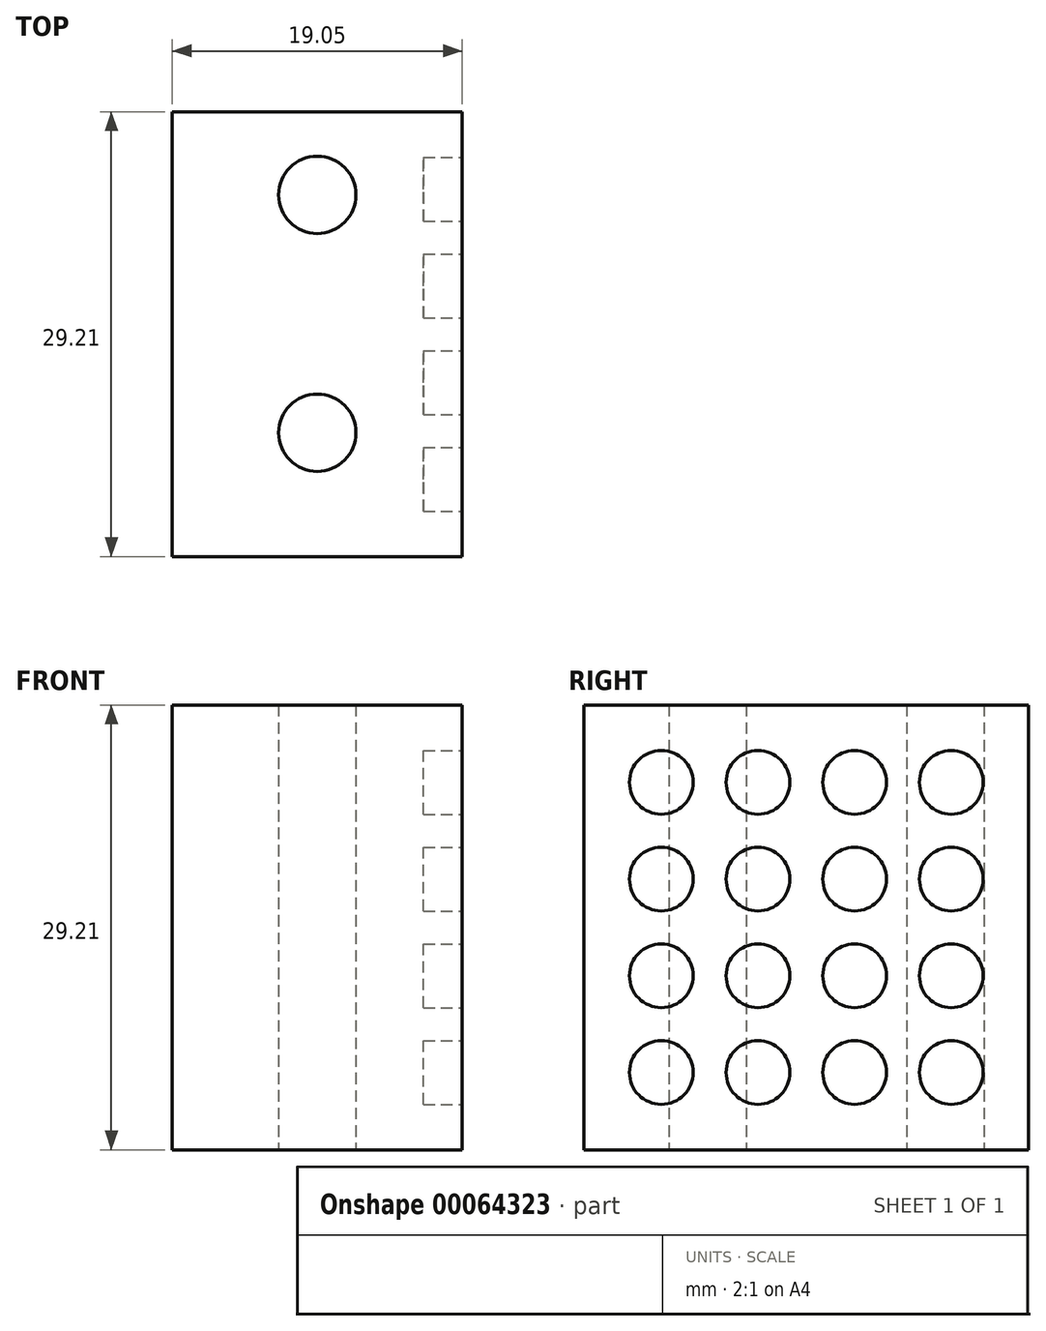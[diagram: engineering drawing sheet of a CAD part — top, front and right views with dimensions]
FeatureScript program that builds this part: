
annotation { "Feature Type Name" : "Feature", "Feature Type Description" : "" }
export const myFeature = defineFeature(function(context is Context, id is Id, definition is map)
    precondition{}
    {
        {
            var Q0;
            Q0=qCreatedBy(makeId("Top.planeOp"),FACE);
            var sketch = newSketch(context, id + "F0", { "sketchPlane" : qUnion([Q0])});
            skLineSegment(sketch, "E0.bottom", {"start": v(0, 0) * mm, "end": v(-19.05, 0) * mm});
            skLineSegment(sketch, "E0.top", {"start": v(0, 29.21) * mm, "end": v(-19.05, 29.21) * mm});
            skLineSegment(sketch, "E0.left", {"start": v(0, 0) * mm, "end": v(0, 29.21) * mm});
            skLineSegment(sketch, "E0.right", {"start": v(-19.05, 0) * mm, "end": v(-19.05, 29.21) * mm});
            skCircle(sketch, "E1", {"center": v(-9.53, 23.75) * mm, "radius": 2.54 * mm});
            skCircle(sketch, "E2", {"center": v(-9.53, 8.13) * mm, "radius": 2.54 * mm});
            skLineSegment(sketch, "E3", {"start": v(-9.53, 29.21) * mm, "end": v(-9.53, 0) * mm, "construction": true});
            skSolve(sketch);
        }
        {
            var Q0;
            Q0 = qSketchRegion(id + "F0", true);
            extrude(context, id + "F1", {"entities" : qUnion([Q0]), "depth" : 29.2 * mm});
        }
        {
            var Q0;
            Q0=makeQuery(id+"F1.opExtrude","SWEPT_FACE",FACE,{"disambiguationData":[OSD([sQuery(id+"F0.wireOp",EDGE,"E0.left")])]});
            var sketch = newSketch(context, id + "F2", { "sketchPlane" : qUnion([Q0])});
            skCircle(sketch, "E4", {"center": v(5.08, 24.13) * mm, "radius": 2.1 * mm});
            skCircle(sketch, "E5.1.0.0", {"center": v(11.43, 24.13) * mm, "radius": 2.1 * mm});
            skCircle(sketch, "E5.2.0.0", {"center": v(17.78, 24.13) * mm, "radius": 2.1 * mm});
            skCircle(sketch, "E5.3.0.0", {"center": v(24.13, 24.13) * mm, "radius": 2.1 * mm});
            skLineSegment(sketch, "E5.direction1", {"start": v(5.08, 24.13) * mm, "end": v(11.43, 24.13) * mm, "construction": true});
            skLineSegment(sketch, "E6.1.0.0", {"start": v(5.08, 17.78) * mm, "end": v(11.43, 17.78) * mm, "construction": true});
            skCircle(sketch, "E6.1.0.1", {"center": v(24.13, 17.78) * mm, "radius": 2.1 * mm});
            skCircle(sketch, "E6.1.0.2", {"center": v(17.78, 17.78) * mm, "radius": 2.1 * mm});
            skCircle(sketch, "E6.1.0.3", {"center": v(11.43, 17.78) * mm, "radius": 2.1 * mm});
            skCircle(sketch, "E6.1.0.4", {"center": v(5.08, 17.78) * mm, "radius": 2.1 * mm});
            skLineSegment(sketch, "E6.2.0.0", {"start": v(5.08, 11.43) * mm, "end": v(11.43, 11.43) * mm, "construction": true});
            skCircle(sketch, "E6.2.0.1", {"center": v(24.13, 11.43) * mm, "radius": 2.1 * mm});
            skCircle(sketch, "E6.2.0.2", {"center": v(17.78, 11.43) * mm, "radius": 2.1 * mm});
            skCircle(sketch, "E6.2.0.3", {"center": v(11.43, 11.43) * mm, "radius": 2.1 * mm});
            skCircle(sketch, "E6.2.0.4", {"center": v(5.08, 11.43) * mm, "radius": 2.1 * mm});
            skLineSegment(sketch, "E6.3.0.0", {"start": v(5.08, 5.08) * mm, "end": v(11.43, 5.08) * mm, "construction": true});
            skCircle(sketch, "E6.3.0.1", {"center": v(24.13, 5.08) * mm, "radius": 2.1 * mm});
            skCircle(sketch, "E6.3.0.2", {"center": v(17.78, 5.08) * mm, "radius": 2.1 * mm});
            skCircle(sketch, "E6.3.0.3", {"center": v(11.43, 5.08) * mm, "radius": 2.1 * mm});
            skCircle(sketch, "E6.3.0.4", {"center": v(5.08, 5.08) * mm, "radius": 2.1 * mm});
            skLineSegment(sketch, "E6.direction1", {"start": v(5.08, 24.13) * mm, "end": v(5.08, 17.78) * mm, "construction": true});
            skSolve(sketch);
        }
        {
            var Q0;
            Q0 = qSketchRegion(id + "F2", true);
            extrude(context, id + "F3", {"entities" : qUnion([Q0]), "operationType" : NewBodyOperationType.REMOVE, "oppositeDirection" : true, "depth" : 2.54 * mm});
        }
    });
